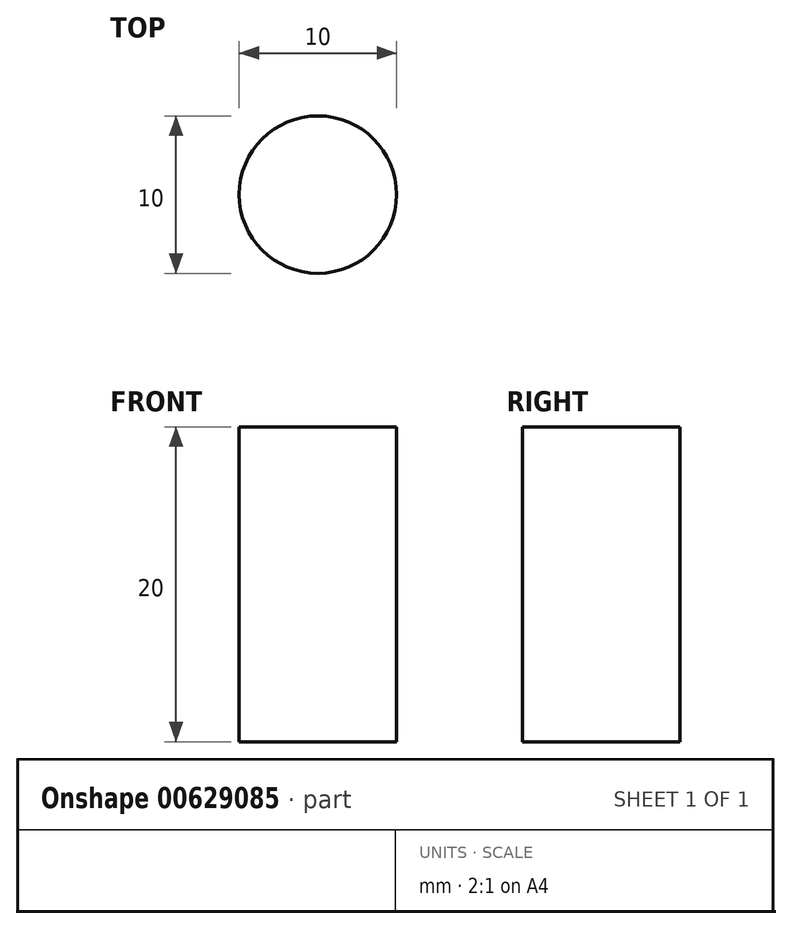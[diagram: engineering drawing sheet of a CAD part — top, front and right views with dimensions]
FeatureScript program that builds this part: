
annotation { "Feature Type Name" : "Feature", "Feature Type Description" : "" }
export const myFeature = defineFeature(function(context is Context, id is Id, definition is map)
    precondition{}
    {
        {
            var Q0;
            Q0=qCreatedBy(makeId("Top.planeOp"),FACE);
            var sketch = newSketch(context, id + "F0", { "sketchPlane" : qUnion([Q0])});
            skCircle(sketch, "E0", {"center": v(0, 0) * mm, "radius": 5 * mm});
            skSolve(sketch);
        }
        {
            var Q0;
            Q0=makeQuery(id+"F0.imprint","IMPRINT",FACE,{"disambiguationData":[TD([[makeQuery(id+"F0.imprint","IMPRINT",EDGE,{"derivedFrom":sQuery(id+"F0.wireOp",EDGE,"E0")}),1.0]])]});
            extrude(context, id + "F1", {"entities" : qUnion([Q0]), "depth" : 20 * mm, "offsetDistance" : 25 * mm, "symmetric" : true});
        }
    });
